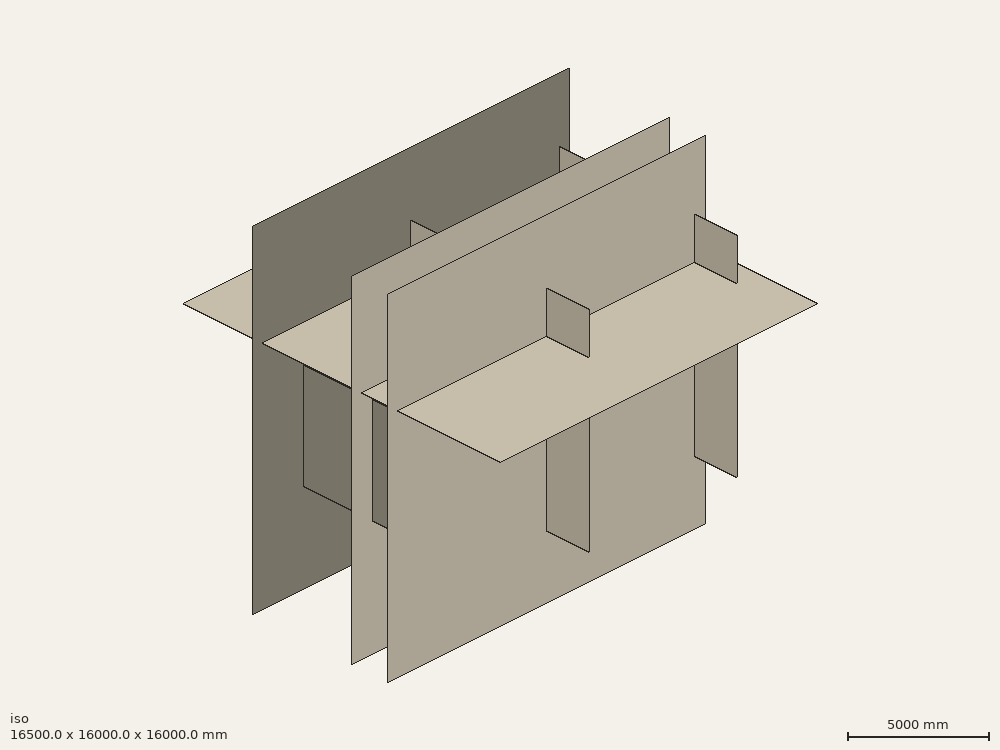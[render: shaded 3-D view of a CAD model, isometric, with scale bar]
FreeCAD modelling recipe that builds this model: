
FCSTD DOCUMENT  (FreeCAD 0.17R13509 (Git))
Label: 1806_fontderibes
License: CreativeCommons Attribution
LicenseURL: http://creativecommons.org/licenses/by/4.0/
objects: App::FeaturePython×61, Part::Part2DObjectPython×29, Part::FeaturePython×25, App::DocumentObjectGroup×16, Sketcher::SketchObject×9, Part::Extrusion×7, App::MaterialObjectPython×6, TechDraw::DrawViewArch×6, App::DocumentObjectGroupPython×4, Spreadsheet::Sheet×1, TechDraw::DrawSVGTemplate×1, Part::Feature×1, TechDraw::DrawViewAnnotation×1, TechDraw::DrawPage×1
note: 79 computed .brp shape members not serialized (recipe doc carries the construction recipe); baked Part::Feature solids carry a one-line shape summary decoded from their .brp

FEATURE [Part::Part2DObjectPython] Rectangle014  label="Area bany"  # Draft 2D object (typed FeaturePython)
  ChamferSize = 0
  Columns = 1
  FilletRadius = 0
  Height = 1500
  Length = 2100
  MakeFace = false
  Placement = pos=(5850,-1750,0) rot=(0,0,1;0rad)
  Rows = 1
FEATURE [Part::Part2DObjectPython] Rectangle017  label="Area magatzem"  # Draft 2D object (typed FeaturePython)
  ChamferSize = 0
  Columns = 1
  FilletRadius = 0
  Height = 1500
  Length = 1800
  MakeFace = false
  Placement = pos=(3950,-1750,0) rot=(0,0,1;0rad)
  Rows = 1
FEATURE [Part::Part2DObjectPython] Rectangle019  label="Area cuina"  # Draft 2D object (typed FeaturePython)
  ChamferSize = 0
  Columns = 1
  FilletRadius = 0
  Height = 1500
  Length = 3600
  MakeFace = false
  Placement = pos=(250,-1750,0) rot=(0,0,1;0rad)
  Rows = 1
FEATURE [Part::Part2DObjectPython] Rectangle064  label="Enva_001"  # Draft 2D object (typed FeaturePython)
  ChamferSize = 0
  Columns = 1
  FilletRadius = 0
  Height = 100
  Length = 7900
  MakeFace = true
  Placement = pos=(150,-5350,0) rot=(0,0,1;0rad)
  Rows = 1
FEATURE [Part::Part2DObjectPython] Rectangle073  label="PC_001"  # Draft 2D object (typed FeaturePython)
  ChamferSize = 0
  Columns = 1
  FilletRadius = 0
  Height = 50
  Length = 900
  MakeFace = true
  Placement = pos=(7150,-1925,0) rot=(0,0,1;0rad)
  Rows = 1
FEATURE [Part::Part2DObjectPython] Rectangle074  label="PC_002"  # Draft 2D object (typed FeaturePython)
  ChamferSize = 0
  Columns = 1
  FilletRadius = 0
  Height = 50
  Length = 900
  MakeFace = true
  Placement = pos=(5150,-1925,0) rot=(0,0,1;0rad)
  Rows = 1
FEATURE [Part::Part2DObjectPython] Rectangle075  label="PC_003"  # Draft 2D object (typed FeaturePython)
  ChamferSize = 0
  Columns = 1
  FilletRadius = 0
  Height = 50
  Length = 1500
  MakeFace = true
  Placement = pos=(2650,-1925,0) rot=(0,0,1;0rad)
  Rows = 1
FEATURE [Part::Part2DObjectPython] Arc  # Draft 2D object (typed FeaturePython)
  FirstAngle = 90
  LastAngle = 180
  MakeFace = false
  Placement = pos=(0,-5350,0) rot=(0,0,1;0rad)
  Radius = 3500
FEATURE [Part::Part2DObjectPython] DWire007  label="Enva_002"  # Draft 2D object (typed FeaturePython)
  ChamferSize = 0
  Closed = true
  End = (1350,-1850,0)
  FilletRadius = 0
  Length = 37800
  MakeFace = true
  Placement = pos=(7448.88,13200.2,0) rot=(0,0,1;0rad)
  Points = (28) [(-6098.88,-14950.2,0),(-7198.88,-14950.2,0),(-7198.88,-13450.2,0),(-3598.88,-13450.2,0),(-3598.88,-14950.2,0),(-4698.88,-14950.2,0),+22 more]
  Start = (1350,-1750,0)
  Subdivisions = 0
FEATURE [Part::Part2DObjectPython] Rectangle  label="Area_sala"  # Draft 2D object (typed FeaturePython)
  ChamferSize = 0
  Columns = 1
  FilletRadius = 0
  Height = 3400
  Length = 7900
  MakeFace = false
  Placement = pos=(150,-5250,0) rot=(0,0,1;0rad)
  Rows = 1
FEATURE [Part::Part2DObjectPython] Rectangle047  label="DV_llit"  # Draft 2D object (typed FeaturePython)
  ChamferSize = 0
  Columns = 1
  FilletRadius = 0
  Height = 1800
  Length = 50
  MakeFace = true
  Placement = pos=(5183.23,-4650,0) rot=(0,0,1;0rad)
  Rows = 1
FEATURE [Part::Extrusion] Extrusion  label="PC03_base"
  Base = -> Rectangle075
  Dir = (0,0,2500)
  DirMode = 0
  FaceMakerClass = Part::FaceMakerBullseye
  LengthFwd = 0
  LengthRev = 0
  Solid = true
  Symmetric = false
FEATURE [Part::Extrusion] Extrusion001  label="PC02_base"
  Base = -> Rectangle074
  Dir = (0,0,2500)
  DirMode = 0
  FaceMakerClass = Part::FaceMakerBullseye
  LengthFwd = 0
  LengthRev = 0
  Solid = true
  Symmetric = false
FEATURE [Part::Extrusion] Extrusion002  label="PC_01_base"
  Base = -> Rectangle073
  Dir = (0,0,2500)
  DirMode = 0
  FaceMakerClass = Part::FaceMakerBullseye
  LengthFwd = 0
  LengthRev = 0
  Solid = true
  Symmetric = false
FEATURE [Part::Part2DObjectPython] DWire  # Draft 2D object (typed FeaturePython)
  ChamferSize = 0
  Closed = true
  End = (250,-1750,0)
  FilletRadius = 0
  Length = 41200
  MakeFace = false
  Placement = pos=(7448.88,13200.2,0) rot=(0,0,1;0rad)
  Points = (28) [(-7198.88,-13450.2,0),(-3598.88,-13450.2,0),(-3598.88,-14950.2,0),(-4698.88,-14950.2,0),(-4698.88,-15050.2,0),(-2998.88,-15050.2,0),+22 more]
  Start = (250,-250,0)
  Subdivisions = 0
FEATURE [Spreadsheet::Sheet] IfcProperties  label="GuBIMClass v.1.2_CA"
  cells = A1=Nivell 1; B1=Nivell 2; C1=Nivell 3; D1=Nivell 4; E1=Codi Complert; F1=Descripció; A2=20; B2=10; C2=10; D2=20; E2=2.10.10.20; F2=Sabates
FEATURE [App::DocumentObjectGroup] IfcPropertiesContainer
  Group = -> [IfcProperties]
FEATURE [Part::Part2DObjectPython] Rectangle061  label="area total_base"  # Draft 2D object (typed FeaturePython)
  ChamferSize = 0
  Columns = 1
  FilletRadius = 0
  Height = 5500
  Length = 8200
  MakeFace = false
  Placement = pos=(4.999e-09,-5500,0) rot=(0,0,1;0rad)
  Rows = 1
FEATURE [Sketcher::SketchObject] Sketch006  label="Area total"
  ExternalGeometry = -> [Rectangle061]
  Placement = pos=(7448.88,13200.2,0) rot=(0,0,1;0rad)
  Support = -> [Rectangle061]
  sketch-geometry (4):
    g0: LineSegment StartX=-7448.88 StartY=-18700.2 StartZ=0 EndX=-7448.88 EndY=-13200.2 EndZ=0
    g1: LineSegment StartX=-7448.88 StartY=-13200.2 StartZ=0 EndX=751.125 EndY=-13200.2 EndZ=0
    g2: LineSegment StartX=751.125 StartY=-13200.2 StartZ=0 EndX=751.125 EndY=-18700.2 EndZ=0
    g3: LineSegment StartX=751.125 StartY=-18700.2 StartZ=0 EndX=-7448.88 EndY=-18700.2 EndZ=0
  constraints (11):
    c: Coincident(g0,g1)
    c: Coincident(g1,g2)
    c: Coincident(g2,g3)
    c: Coincident(g3,g0)
    c: Vertical(g0)
    c: Vertical(g2)
    c: Horizontal(g1)
    c: Horizontal(g3)
    c: DistanceX(g1,g1) = 8200  'A'
    c: DistanceY(g2,g2) = 5500  'B'
    c: Coincident(g-3,g0)
FEATURE [App::DocumentObjectGroup] Group002  label="Àrees"
  Group = -> [Rectangle061,Rectangle019,Rectangle017,Rectangle014,Rectangle,Sketch006]
FEATURE [Sketcher::SketchObject] Sketch007  label="Mur_001_base"
  ExternalGeometry = -> [Sketch006]
  Placement = pos=(7448.88,13200.2,0) rot=(0,0,1;0rad)
  sketch-geometry (2):
    g0: LineSegment StartX=-10948.9 StartY=-18625.2 StartZ=0 EndX=2476.12 EndY=-18625.2 EndZ=0
    g1: LineSegment StartX=2476.12 StartY=-18625.2 StartZ=0 EndX=2476.12 EndY=-15050.2 EndZ=0
  constraints (7):
    c: Coincident(g0,g1)
    c: Horizontal(g0)
    c: Vertical(g1)
    c: DistanceX(g0,g0) = 13425  'A'
    c: DistanceY(g1,g1) = 3575  'B'
    c: DistanceY(g-3,g0) = 75  'C'
    c: DistanceX(g-4,g1) = 1725  'D'
FEATURE [Sketcher::SketchObject] Sketch008  label="Mur_002_base"
  ExternalGeometry = -> [Sketch006]
  Placement = pos=(7448.88,13200.2,0) rot=(0,0,1;0rad)
  sketch-geometry (3):
    g0: LineSegment StartX=-7373.88 StartY=-18550.2 StartZ=0 EndX=-7373.88 EndY=-13275.2 EndZ=0
    g1: LineSegment StartX=-7373.88 StartY=-13275.2 StartZ=0 EndX=676.125 EndY=-13275.2 EndZ=0
    g2: LineSegment StartX=676.125 StartY=-13275.2 StartZ=0 EndX=676.125 EndY=-18550.2 EndZ=0
  constraints (10):
    c: Coincident(g0,g1)
    c: Coincident(g1,g2)
    c: Horizontal(g1)
    c: Vertical(g0)
    c: Vertical(g2)
    c: DistanceY(g0,g-6) = 75
    c: DistanceX(g-6,g0) = 75
    c: Equal(g0,g2)
    c: DistanceX(g1,g-4) = 75
    c: DistanceY(g2,g2) = 5275
FEATURE [Sketcher::SketchObject] Sketch009  label="Solera_base"
  ExternalGeometry = -> [Sketch006]
  MapMode = 2
  Placement = pos=(150,-5350,0) rot=(0,0,1;0rad)
  sketch-geometry (4):
    g0: LineSegment StartX=-5.002e-09 StartY=5200 StartZ=0 EndX=7900 EndY=5200 EndZ=0
    g1: LineSegment StartX=7900 StartY=5200 StartZ=0 EndX=7900 EndY=-5.0004e-08 EndZ=0
    g2: LineSegment StartX=7900 StartY=-5.0004e-08 StartZ=0 EndX=-5.002e-09 EndY=-5.0004e-08 EndZ=0
    g3: LineSegment StartX=-5.002e-09 StartY=-5.0004e-08 StartZ=0 EndX=-5.002e-09 EndY=5200 EndZ=0
  constraints (12):
    c: Coincident(g0,g1)
    c: Coincident(g1,g2)
    c: Coincident(g2,g3)
    c: Coincident(g3,g0)
    c: Horizontal(g0)
    c: Horizontal(g2)
    c: Vertical(g1)
    c: Vertical(g3)
    c: DistanceY(g0,g-6) = 150
    c: DistanceY(g-5,g1) = 150
    c: DistanceX(g0,g-4) = 150
    c: DistanceX(g-6,g2) = 150
FEATURE [Sketcher::SketchObject] Sketch010  label="Sabata_001_base"
  ExternalGeometry = -> [Sketch007]
  MapMode = 2
  Placement = pos=(7448.88,13200.2,0) rot=(0,0,1;0rad)
  sketch-geometry (6):
    g0: LineSegment StartX=-11098.9 StartY=-18225.2 StartZ=0 EndX=2076.12 EndY=-18225.2 EndZ=0
    g1: LineSegment StartX=2076.12 StartY=-18225.2 StartZ=0 EndX=2076.12 EndY=-14900.2 EndZ=0
    g2: LineSegment StartX=2076.12 StartY=-14900.2 StartZ=0 EndX=2876.12 EndY=-14900.2 EndZ=0
    g3: LineSegment StartX=2876.12 StartY=-14900.2 StartZ=0 EndX=2876.12 EndY=-19025.2 EndZ=0
    g4: LineSegment StartX=2876.12 StartY=-19025.2 StartZ=0 EndX=-11098.9 EndY=-19025.2 EndZ=0
    g5: LineSegment StartX=-11098.9 StartY=-19025.2 StartZ=0 EndX=-11098.9 EndY=-18225.2 EndZ=0
  constraints (18):
    c: Coincident(g0,g1)
    c: Coincident(g1,g2)
    c: Coincident(g2,g3)
    c: Coincident(g3,g4)
    c: Horizontal(g4)
    c: Coincident(g4,g5)
    c: Coincident(g5,g0)
    c: Vertical(g5)
    c: Vertical(g3)
    c: Vertical(g1)
    c: Horizontal(g2)
    c: Horizontal(g0)
    c: DistanceX(g1,g-3) = 400
    c: DistanceX(g-3,g2) = 400
    c: DistanceY(g-4,g0) = 400
    c: DistanceY(g4,g-4) = 400
    c: DistanceY(g-3,g1) = 150
    c: DistanceX(g0,g-4) = 150
FEATURE [Sketcher::SketchObject] Sketch011  label="Sabata_002_base"
  ExternalGeometry = -> [Sketch008,Sketch007]
  Placement = pos=(7448.88,13200.2,0) rot=(0,0,1;0rad)
  sketch-geometry (8):
    g0: LineSegment StartX=-7773.88 StartY=-18225.2 StartZ=0 EndX=-7773.88 EndY=-12875.2 EndZ=0
    g1: LineSegment StartX=-7773.88 StartY=-12875.2 StartZ=0 EndX=1076.12 EndY=-12875.2 EndZ=0
    g2: LineSegment StartX=1076.12 StartY=-12875.2 StartZ=0 EndX=1076.12 EndY=-18225.2 EndZ=0
    g3: LineSegment StartX=1076.12 StartY=-18225.2 StartZ=0 EndX=276.125 EndY=-18225.2 EndZ=0
    g4: LineSegment StartX=276.125 StartY=-18225.2 StartZ=0 EndX=276.125 EndY=-13675.2 EndZ=0
    g5: LineSegment StartX=276.125 StartY=-13675.2 StartZ=0 EndX=-6973.88 EndY=-13675.2 EndZ=0
    g6: LineSegment StartX=-6973.88 StartY=-13675.2 StartZ=0 EndX=-6973.88 EndY=-18225.2 EndZ=0
    g7: LineSegment StartX=-6973.88 StartY=-18225.2 StartZ=0 EndX=-7773.88 EndY=-18225.2 EndZ=0
  constraints (25):
    c: Coincident(g0,g1)
    c: Coincident(g1,g2)
    c: Coincident(g2,g3)
    c: Coincident(g3,g4)
    c: Coincident(g4,g5)
    c: Coincident(g5,g6)
    c: Coincident(g6,g7)
    c: Coincident(g7,g0)
    c: Horizontal(g7)
    c: Horizontal(g3)
    c: Horizontal(g5)
    c: Horizontal(g1)
    c: Vertical(g0)
    c: Vertical(g6)
    c: Vertical(g4)
    c: Vertical(g2)
    c: Equal(g6,g4)
    c: Equal(g2,g0)
    c: DistanceY(g-5,g0) = 400
    c: DistanceY(g5,g-5) = 400
    c: DistanceX(g0,g-5) = 400
    c: DistanceX(g-5,g6) = 400
    c: DistanceY(g0,g-6) = -400
    c: Equal(g3,g7)
    c: DistanceX(g3,g-3) = 400
FEATURE [Sketcher::SketchObject] Sketch
  Placement = pos=(8200,-5350,0) rot=(0.57735,0.57735,0.57735;2.0944rad)
  sketch-geometry (24):
    g0: LineSegment StartX=0 StartY=0 StartZ=0 EndX=3400 EndY=0 EndZ=0
    g1: LineSegment StartX=3400 StartY=0 StartZ=0 EndX=3400 EndY=2500 EndZ=0
    g2: LineSegment StartX=3400 StartY=2500 StartZ=0 EndX=0 EndY=2500 EndZ=0
    g3: LineSegment StartX=0 StartY=2500 StartZ=0 EndX=0 EndY=0 EndZ=0
    g4: LineSegment StartX=30 StartY=30 StartZ=0 EndX=3370 EndY=30 EndZ=0
    g5: LineSegment StartX=3370 StartY=30 StartZ=0 EndX=3370 EndY=2470 EndZ=0
    g6: LineSegment StartX=3370 StartY=2470 StartZ=0 EndX=30 EndY=2470 EndZ=0
    g7: LineSegment StartX=30 StartY=2470 StartZ=0 EndX=30 EndY=30 EndZ=0
    g8: LineSegment StartX=33 StartY=33 StartZ=0 EndX=1698.5 EndY=33 EndZ=0
    g9: LineSegment StartX=1698.5 StartY=33 StartZ=0 EndX=1698.5 EndY=2467 EndZ=0
    g10: LineSegment StartX=1698.5 StartY=2467 StartZ=0 EndX=33 EndY=2467 EndZ=0
    g11: LineSegment StartX=33 StartY=2467 StartZ=0 EndX=33 EndY=33 EndZ=0
    g12: LineSegment StartX=103 StartY=103 StartZ=0 EndX=1628.5 EndY=103 EndZ=0
    g13: LineSegment StartX=1628.5 StartY=103 StartZ=0 EndX=1628.5 EndY=2397 EndZ=0
    g14: LineSegment StartX=1628.5 StartY=2397 StartZ=0 EndX=103 EndY=2397 EndZ=0
    g15: LineSegment StartX=103 StartY=2397 StartZ=0 EndX=103 EndY=103 EndZ=0
    g16: LineSegment StartX=1701.5 StartY=33 StartZ=0 EndX=3367 EndY=33 EndZ=0
    g17: LineSegment StartX=3367 StartY=33 StartZ=0 EndX=3367 EndY=2467 EndZ=0
    g18: LineSegment StartX=3367 StartY=2467 StartZ=0 EndX=1701.5 EndY=2467 EndZ=0
    g19: LineSegment StartX=1701.5 StartY=2467 StartZ=0 EndX=1701.5 EndY=33 EndZ=0
    g20: LineSegment StartX=1771.5 StartY=103 StartZ=0 EndX=3297 EndY=103 EndZ=0
    g21: LineSegment StartX=3297 StartY=103 StartZ=0 EndX=3297 EndY=2397 EndZ=0
    g22: LineSegment StartX=3297 StartY=2397 StartZ=0 EndX=1771.5 EndY=2397 EndZ=0
    g23: LineSegment StartX=1771.5 StartY=2397 StartZ=0 EndX=1771.5 EndY=103 EndZ=0
  constraints (71):
    c: Coincident(g0,g1)
    c: Coincident(g1,g2)
    c: Coincident(g2,g3)
    c: Coincident(g3,g0)
    c: Horizontal(g0)
    c: Horizontal(g2)
    c: Vertical(g1)
    c: Vertical(g3)
    c: Coincident(g4,g5)
    c: Coincident(g5,g6)
    c: Coincident(g6,g7)
    c: Coincident(g7,g4)
    c: Horizontal(g4)
    c: Horizontal(g6)
    c: Vertical(g5)
    c: Vertical(g7)
    c: DistanceY(g1) = 2500  'Height'
    c: DistanceX(g0) = 3400  'Width'
    c: DistanceY(g6,g2) = 30
    c: DistanceX(g2,g6) = 30
    c: DistanceX(g4,g0) = 30
    c: DistanceY(g0,g4) = 30
    c: Coincident(g0,g-1)
    c: Coincident(g8,g9)
    c: Coincident(g9,g10)
    c: Coincident(g10,g11)
    c: Coincident(g11,g8)
    c: Horizontal(g8)
    c: Horizontal(g10)
    c: Vertical(g9)
    c: Vertical(g11)
    c: Coincident(g12,g13)
    c: Coincident(g13,g14)
    c: Coincident(g14,g15)
    c: Coincident(g15,g12)
    c: Horizontal(g12)
    c: Horizontal(g14)
    c: Vertical(g13)
    c: Vertical(g15)
    c: Coincident(g16,g17)
    c: Coincident(g17,g18)
    c: Coincident(g18,g19)
    c: Coincident(g19,g16)
    c: Horizontal(g16)
    c: Horizontal(g18)
    c: Vertical(g17)
    c: Vertical(g19)
    c: Coincident(g20,g21)
    c: Coincident(g21,g22)
    c: Coincident(g22,g23)
    c: Coincident(g23,g20)
    c: Horizontal(g20)
    c: Horizontal(g22)
    c: Vertical(g21)
    c: Vertical(g23)
    c: DistanceY(g8,g12) = 70
    c: DistanceX(g8,g12) = 70
    c: DistanceX(g21,g17) = 70
    c: DistanceY(g21,g17) = 70
    c: DistanceX(g16,g20) = 70
    c: DistanceX(g14,g10) = 70
    c: Equal(g22,g14)
    c: DistanceY(g8,g16) = 0
    c: DistanceY(g10,g18) = 0
    c: DistanceX(g4,g8) = 3
    c: DistanceY(g4,g8) = 3
    c: DistanceX(g6,g18) = -3
    c: DistanceY(g6,g18) = -3
    c: DistanceX(g9,g19) = 3
    c: PointOnObject(g13,g22)
    c: PointOnObject(g12,g20)
FEATURE [Sketcher::SketchObject] Sketch012
  Placement = pos=(1e-12,-1850,0) rot=(0.57735,-0.57735,-0.57735;2.0944rad)
  sketch-geometry (24):
    g0: LineSegment StartX=0 StartY=0 StartZ=0 EndX=3500 EndY=0 EndZ=0
    g1: LineSegment StartX=3500 StartY=0 StartZ=0 EndX=3500 EndY=2500 EndZ=0
    g2: LineSegment StartX=3500 StartY=2500 StartZ=0 EndX=0 EndY=2500 EndZ=0
    g3: LineSegment StartX=0 StartY=2500 StartZ=0 EndX=0 EndY=0 EndZ=0
    g4: LineSegment StartX=30 StartY=30 StartZ=0 EndX=3470 EndY=30 EndZ=0
    g5: LineSegment StartX=3470 StartY=30 StartZ=0 EndX=3470 EndY=2470 EndZ=0
    g6: LineSegment StartX=3470 StartY=2470 StartZ=0 EndX=30 EndY=2470 EndZ=0
    g7: LineSegment StartX=30 StartY=2470 StartZ=0 EndX=30 EndY=30 EndZ=0
    g8: LineSegment StartX=33 StartY=33 StartZ=0 EndX=1748.5 EndY=33 EndZ=0
    g9: LineSegment StartX=1748.5 StartY=33 StartZ=0 EndX=1748.5 EndY=2467 EndZ=0
    g10: LineSegment StartX=1748.5 StartY=2467 StartZ=0 EndX=33 EndY=2467 EndZ=0
    g11: LineSegment StartX=33 StartY=2467 StartZ=0 EndX=33 EndY=33 EndZ=0
    g12: LineSegment StartX=103 StartY=103 StartZ=0 EndX=1678.5 EndY=103 EndZ=0
    g13: LineSegment StartX=1678.5 StartY=103 StartZ=0 EndX=1678.5 EndY=2397 EndZ=0
    g14: LineSegment StartX=1678.5 StartY=2397 StartZ=0 EndX=103 EndY=2397 EndZ=0
    g15: LineSegment StartX=103 StartY=2397 StartZ=0 EndX=103 EndY=103 EndZ=0
    g16: LineSegment StartX=1751.5 StartY=33 StartZ=0 EndX=3467 EndY=33 EndZ=0
    g17: LineSegment StartX=3467 StartY=33 StartZ=0 EndX=3467 EndY=2467 EndZ=0
    g18: LineSegment StartX=3467 StartY=2467 StartZ=0 EndX=1751.5 EndY=2467 EndZ=0
    g19: LineSegment StartX=1751.5 StartY=2467 StartZ=0 EndX=1751.5 EndY=33 EndZ=0
    g20: LineSegment StartX=1821.5 StartY=103 StartZ=0 EndX=3397 EndY=103 EndZ=0
    g21: LineSegment StartX=3397 StartY=103 StartZ=0 EndX=3397 EndY=2397 EndZ=0
    g22: LineSegment StartX=3397 StartY=2397 StartZ=0 EndX=1821.5 EndY=2397 EndZ=0
    g23: LineSegment StartX=1821.5 StartY=2397 StartZ=0 EndX=1821.5 EndY=103 EndZ=0
  constraints (71):
    c: Coincident(g0,g1)
    c: Coincident(g1,g2)
    c: Coincident(g2,g3)
    c: Coincident(g3,g0)
    c: Horizontal(g0)
    c: Horizontal(g2)
    c: Vertical(g1)
    c: Vertical(g3)
    c: Coincident(g4,g5)
    c: Coincident(g5,g6)
    c: Coincident(g6,g7)
    c: Coincident(g7,g4)
    c: Horizontal(g4)
    c: Horizontal(g6)
    c: Vertical(g5)
    c: Vertical(g7)
    c: DistanceY(g1) = 2500  'Height'
    c: DistanceX(g0) = 3500  'Width'
    c: DistanceY(g6,g2) = 30
    c: DistanceX(g2,g6) = 30
    c: DistanceX(g4,g0) = 30
    c: DistanceY(g0,g4) = 30
    c: Coincident(g0,g-1)
    c: Coincident(g8,g9)
    c: Coincident(g9,g10)
    c: Coincident(g10,g11)
    c: Coincident(g11,g8)
    c: Horizontal(g8)
    c: Horizontal(g10)
    c: Vertical(g9)
    c: Vertical(g11)
    c: Coincident(g12,g13)
    c: Coincident(g13,g14)
    c: Coincident(g14,g15)
    c: Coincident(g15,g12)
    c: Horizontal(g12)
    c: Horizontal(g14)
    c: Vertical(g13)
    c: Vertical(g15)
    c: Coincident(g16,g17)
    c: Coincident(g17,g18)
    c: Coincident(g18,g19)
    c: Coincident(g19,g16)
    c: Horizontal(g16)
    c: Horizontal(g18)
    c: Vertical(g17)
    c: Vertical(g19)
    c: Coincident(g20,g21)
    c: Coincident(g21,g22)
    c: Coincident(g22,g23)
    c: Coincident(g23,g20)
    c: Horizontal(g20)
    c: Horizontal(g22)
    c: Vertical(g21)
    c: Vertical(g23)
    c: DistanceY(g8,g12) = 70
    c: DistanceX(g8,g12) = 70
    c: DistanceX(g21,g17) = 70
    c: DistanceY(g21,g17) = 70
    c: DistanceX(g16,g20) = 70
    c: DistanceX(g14,g10) = 70
    c: Equal(g22,g14)
    c: DistanceY(g8,g16) = 0
    c: DistanceY(g10,g18) = 0
    c: DistanceX(g4,g8) = 3
    c: DistanceY(g4,g8) = 3
    c: DistanceX(g6,g18) = -3
    c: DistanceY(g6,g18) = -3
    c: DistanceX(g9,g19) = 3
    c: PointOnObject(g13,g22)
    c: PointOnObject(g12,g20)
FEATURE [App::MaterialObjectPython] Material  label="Formigó H-25"  # material (typed FeaturePython)
  Material = Color=(0.9411764705882353, 0.9411764705882353, 0.9411764705882353),DiffuseColor=(0.9411764740943909, 0.9411764740943909, 0.9411764740943909),+3 more (map truncated)
  Transparency = 0
FEATURE [Part::FeaturePython] Structure  label="Solera"  # WARN: FeaturePython — macro-defined, semantics opaque (R4)
  Base = -> Sketch009
  FaceMaker = 0
  Height = 200
  HorizontalArea = 41080000
  Length = 0
  Material = -> Material
  MoveWithHost = false
  Nodes = (4) [(-7298.88,-13350.2,0),(601.125,-13350.2,0),(601.125,-18550.2,0),(-7298.88,-18550.2,0)]
  NodesOffset = 0
  Normal = (0,0,0)
  PerimeterLength = 26200
  Placement = pos=(0,0,-300) rot=(0,0,1;0rad)
  Role = 3
  VerticalArea = 5240000
  Width = 100
FEATURE [Part::FeaturePython] Structure001  label="Sabata_001"  # Arch/BIM object (typed FeaturePython)
  Base = -> Sketch010
  FaceMaker = 0
  Height = 400
  HorizontalArea = 13840000
  IfcProperties = -> IfcProperties
  Length = 0
  Material = -> Material
  MoveWithHost = false
  Nodes = (2) [(-2863.62,-18210.5,-313.595),(-2863.62,-18210.5,86.4045)]
  NodesOffset = 0
  Normal = (0,0,0)
  PerimeterLength = 36200
  Placement = pos=(0,0,-500) rot=(0,0,1;0rad)
  Role = 7
  VerticalArea = 14480000
  Width = 100
FEATURE [Part::FeaturePython] Structure002  label="Sabata_002"  # Arch/BIM object (typed FeaturePython)
  Base = -> Sketch011
  FaceMaker = 0
  Height = 400
  HorizontalArea = 14360000
  IfcAttributes = IfcUID=3Gc_ZFGLuHwBQVF1N2v1hf
  IfcProperties = -> IfcProperties
  Length = 0
  Material = -> Material
  MoveWithHost = false
  Nodes = (2) [(-3348.88,-14662.1,-232.343),(-3348.88,-14662.1,-632.343)]
  NodesOffset = 0
  Normal = (0,0,0)
  PerimeterLength = 37500
  Placement = pos=(1e-12,0,-500) rot=(0,0,1;0rad)
  Role = 7
  VerticalArea = 1.5e+07
  Width = 100
FEATURE [App::DocumentObjectGroup] Group008  label="Estructura"
  Group = -> [Structure,Structure001,Structure002]
FEATURE [Part::FeaturePython] Structure003  label="Forjat coberta"  # WARN: FeaturePython — macro-defined, semantics opaque (R4)
  Base = -> Sketch006
  FaceMaker = 0
  Height = 200
  HorizontalArea = 45100000
  Length = 0
  Material = -> Material
  MoveWithHost = false
  Nodes = (4) [(-7448.88,-18700.2,0),(-7448.88,-13200.2,0),(751.125,-13200.2,0),(751.125,-18700.2,0)]
  NodesOffset = 0
  Normal = (0,0,1)
  PerimeterLength = 27400
  Placement = pos=(0,0,2500) rot=(0,0,1;0rad)
  Role = 3
  VerticalArea = 5480000
  Width = 100
FEATURE [Part::FeaturePython] Wall007  label="Muret coberta"  # WARN: FeaturePython — macro-defined, semantics opaque (R4)
  Align = 0
  Base = -> Sketch006
  Face = 0
  Height = 400
  HorizontalArea = 5.32e+06
  Length = 27400
  Material = -> Material
  MoveWithHost = false
  Normal = (0,0,1)
  PerimeterLength = 27400
  Placement = pos=(0,0,2700) rot=(0,0,1;0rad)
  Role = 1
  VerticalArea = 21280000
  Width = 200
FEATURE [App::DocumentObjectGroup] Group009  label="PC_EST"
  Group = -> [Structure003,Wall007]
FEATURE [App::DocumentObjectGroupPython] Floor001  label="Coberta"  # scripted group (container) (typed FeaturePython)
  Area = 0
  Group = -> [Group009]
  Height = 0
FEATURE [App::MaterialObjectPython] Material001  label="Gero"  # material (typed FeaturePython)
  Description = Maó calat de forats perpendiculars al pla (V>10%)
  Material = Color=(1.0, 0.5647058823529412, 0.1843137254901961),Description=Maó calat de forats perpendiculars al pla (V>10%),+4 more (map truncated)
  Transparency = 0
FEATURE [Part::FeaturePython] Wall001  label="Mur_002"  # Arch/BIM object (typed FeaturePython)
  Align = 2
  Base = -> Sketch008
  Description = Mur de gero
  Face = 0
  Height = 3000
  HorizontalArea = 2.79e+06
  IfcAttributes = IfcUID=0CiF5mFoOHwBg6F1N2v1hf
  Length = 18600
  Material = -> Material001
  MoveWithHost = false
  Normal = (0,0,0)
  PerimeterLength = 37500
  Placement = pos=(0,0,-500) rot=(0,0,1;0rad)
  Role = 1
  VerticalArea = 7.8e+07
  Width = 150
FEATURE [Part::FeaturePython] Wall002  label="Mur_001"  # Arch/BIM object (typed FeaturePython)
  Align = 2
  Base = -> Sketch007
  Description = Mur de gero
  Face = 0
  Height = 3000
  HorizontalArea = 2977500
  IfcAttributes = IfcUID=0ChshFFoOHwBdvF1N2v1hf
  Length = 17000
  Material = -> Material001
  MoveWithHost = false
  Normal = (0,0,0)
  PerimeterLength = 34300
  Placement = pos=(0,0,-500) rot=(0,0,1;0rad)
  Role = 1
  VerticalArea = 99120000
  Width = 150
FEATURE [App::DocumentObjectGroup] Group003  label="Murs Ext"
  Group = -> [Wall002,Wall001]
FEATURE [Part::FeaturePython] Window  label="F01_002"  # WARN: FeaturePython — macro-defined, semantics opaque (R4)
  Area = 8500000
  Base = -> Sketch
  Height = 2500
  HoleDepth = 0
  HoleWire = 0
  HorizontalArea = 0
  Hosts = -> [Wall001]
  LouvreSpacing = 0
  LouvreWidth = 0
  MoveWithHost = true
  Normal = (-1,0,0)
  Opening = 0
  PerimeterLength = 0
  Preset = 5
  Role = 1
  SymbolElevation = false
  SymbolPlan = false
  VerticalArea = 0
  Width = 3400
  WindowParts = OuterFrame | Frame | Wire0,Wire1 | 150.0 | 0.0 | LeftFrame | Frame | Wire2,Wire3 | 30.0 | 75.0 | LeftGlass | Glass panel | Wire3 | 3.0 | 90.0 | RightFrame | Frame | Wire4,Wire5 | 30.0 | 105.0 | RightGlass | Glass panel | Wire5 | 3.0 | 120.0
  WindowParts1 = 0
FEATURE [Part::FeaturePython] Window001  label="F01_001"  # WARN: FeaturePython — macro-defined, semantics opaque (R4)
  Area = 8750000
  Base = -> Sketch012
  Height = 2500
  HoleDepth = 0
  HoleWire = 0
  HorizontalArea = 0
  Hosts = -> [Wall001]
  LouvreSpacing = 0
  LouvreWidth = 0
  MoveWithHost = true
  Normal = (1,0,0)
  Opening = 0
  PerimeterLength = 0
  Preset = 5
  Role = 1
  SymbolElevation = false
  SymbolPlan = false
  VerticalArea = 0
  Width = 3500
  WindowParts = OuterFrame | Frame | Wire0,Wire1 | 150.0 | 0.0 | LeftFrame | Frame | Wire2,Wire3 | 30.0 | 75.0 | LeftGlass | Glass panel | Wire3 | 3.0 | 90.0 | RightFrame | Frame | Wire4,Wire5 | 30.0 | 105.0 | RightGlass | Glass panel | Wire5 | 3.0 | 120.0
  WindowParts1 = 0
FEATURE [Sketcher::SketchObject] Sketch013
  ExternalGeometry = -> [Wall002]
  MapMode = 5
  Placement = pos=(7448.88,-5500,-500) rot=(1,0,0;1.5708rad)
  sketch-geometry (8):
    g0: LineSegment StartX=-5073.88 StartY=2100 StartZ=0 EndX=-2223.88 EndY=2100 EndZ=0
    g1: LineSegment StartX=-2223.88 StartY=2100 StartZ=0 EndX=-2223.88 EndY=1400 EndZ=0
    g2: LineSegment StartX=-2223.88 StartY=1400 StartZ=0 EndX=-5073.88 EndY=1400 EndZ=0
    g3: LineSegment StartX=-5073.88 StartY=1400 StartZ=0 EndX=-5073.88 EndY=2100 EndZ=0
    g4: LineSegment StartX=-5043.88 StartY=2070 StartZ=0 EndX=-2253.88 EndY=2070 EndZ=0
    g5: LineSegment StartX=-2253.88 StartY=2070 StartZ=0 EndX=-2253.88 EndY=1430 EndZ=0
    g6: LineSegment StartX=-2253.88 StartY=1430 StartZ=0 EndX=-5043.88 EndY=1430 EndZ=0
    g7: LineSegment StartX=-5043.88 StartY=1430 StartZ=0 EndX=-5043.88 EndY=2070 EndZ=0
  constraints (24):
    c: Coincident(g0,g1)
    c: Coincident(g1,g2)
    c: Coincident(g2,g3)
    c: Coincident(g3,g0)
    c: Horizontal(g0)
    c: Horizontal(g2)
    c: Vertical(g1)
    c: Vertical(g3)
    c: Coincident(g4,g5)
    c: Coincident(g5,g6)
    c: Coincident(g6,g7)
    c: Coincident(g7,g4)
    c: Horizontal(g4)
    c: Horizontal(g6)
    c: Vertical(g5)
    c: Vertical(g7)
    c: DistanceX(g0,g4) = 30
    c: DistanceX(g5,g1) = 30
    c: DistanceY(g4,g0) = 30
    c: DistanceY(g2,g6) = 30
    c: DistanceX(g2,g2) = 2850
    c: DistanceY(g1,g1) = 700
    c: DistanceX(g-4,g0) = 5875
    c: DistanceY(g0,g-4) = 900
FEATURE [App::MaterialObjectPython] Material002  label="Fusta vernissada"  # material (typed FeaturePython)
  Material = Color=(0.8117647058823529, 0.403921568627451, 0.0),DiffuseColor=(0.8117647171020508, 0.40392157435417175, 0.0),Name=Fusta vernissada,Transparency=0,+1 more (map truncated)
  Transparency = 0
FEATURE [Part::FeaturePython] Wall004  label="DIV_03"  # WARN: FeaturePython — macro-defined, semantics opaque (R4)
  Align = 2
  Base = -> Rectangle047
  Description = Divisió Vertical de fusta
  Face = 0
  Height = 1800
  HorizontalArea = 90000
  Length = 0
  Material = -> Material002
  MoveWithHost = false
  Normal = (0,0,0)
  PerimeterLength = 3700
  Role = 1
  VerticalArea = 6.66e+06
  Width = 100
FEATURE [Part::FeaturePython] Component  label="PC03"  # Arch/BIM object (typed FeaturePython)
  Base = -> Extrusion
  Description = Porta corredissa
  HorizontalArea = 0
  IfcAttributes = IfcUID=0CidWIFoOHwBntF1N2v1hf
  Material = -> Material002
  MoveWithHost = false
  PerimeterLength = 0
  Role = 6
  VerticalArea = 0
FEATURE [Part::FeaturePython] Component003  label="PC02"  # Arch/BIM object (typed FeaturePython)
  Base = -> Extrusion001
  Description = Porta corredissa
  HorizontalArea = 0
  IfcAttributes = IfcUID=0CizUUFoOHw8DBF1N2v1hf
  Material = -> Material002
  MoveWithHost = false
  PerimeterLength = 0
  Role = 6
  VerticalArea = 0
FEATURE [Part::FeaturePython] Component004  label="PC01"  # Arch/BIM object (typed FeaturePython)
  Base = -> Extrusion002
  Description = Porta corredissa
  HorizontalArea = 0
  IfcAttributes = IfcUID=0CjH0XFoOHwA19F1N2v1hf
  Material = -> Material002
  MoveWithHost = false
  PerimeterLength = 0
  Role = 6
  VerticalArea = 0
FEATURE [App::DocumentObjectGroup] Group004  label="Fusteries Int"
  Group = -> [Rectangle073,Rectangle074,Rectangle075,Component,Component003,Component004]
FEATURE [App::MaterialObjectPython] Material003  label="Acer Corten"  # material (typed FeaturePython)
  Material = Color=(0.6666666666666666, 0.0, 0.0); DiffuseColor=(0.6666666865348816, 0.0, 0.0); Name=Acer Corten; Transparency=0; ViewColor=(0.6666666666666666, 0.0, 0.0)
  Transparency = 0
FEATURE [Part::FeaturePython] Component006  label="S01_001"  # Arch/BIM object (typed FeaturePython)
  HorizontalArea = 0
  IfcAttributes = IfcUID=1ywVmYGP8Hw8cSF1N2v1hf
  Material = -> Material003
  MoveWithHost = false
  PerimeterLength = 0
  Placement = pos=(8200,-1850,0) rot=(0,0,-1;1.5708rad)
  Role = 13
  VerticalArea = 0
FEATURE [Part::FeaturePython] Component007  label="S01_002"  # Arch/BIM object (typed FeaturePython)
  CloneOf = -> Component006
  Description = Fusteria d'alumini corredissa
  HorizontalArea = 0
  IfcAttributes = IfcUID=1z4270GP8Hw9ipF1N2v1hf
  Material = -> Material003
  MoveWithHost = false
  PerimeterLength = 0
  Placement = pos=(8200,-5250,0) rot=(0,0,-1;1.5708rad)
  Role = 13
  VerticalArea = 0
FEATURE [Part::FeaturePython] Component008  label="S02"  # Arch/BIM object (typed FeaturePython)
  Description = Fusteria d'alumini corredissa
  HorizontalArea = 0
  IfcAttributes = IfcUID=1z4271GP8HwBOmF1N2v1hf
  Material = -> Material003
  MoveWithHost = false
  PerimeterLength = 0
  Placement = pos=(-3350,-5350,0) rot=(0,0,1;0rad)
  Role = 13
  VerticalArea = 0
FEATURE [App::DocumentObjectGroup] Group006  label="Serralleria"
  Group = -> [Component006,Component007,Component008]
FEATURE [App::MaterialObjectPython] Material004  label="Formigó lliscat"  # material (typed FeaturePython)
  Material = Color=(0.9411764705882353, 0.9411764705882353, 0.9411764705882353),DiffuseColor=(0.9411764740943909, 0.9411764740943909, 0.9411764740943909),+3 more (map truncated)
  Transparency = 0
FEATURE [App::MaterialObjectPython] Material005  label="Enguixat"  # material (typed FeaturePython)
  Material = Color=(1.0, 1.0, 1.0); DiffuseColor=(1.0, 1.0, 1.0); Name=Enguixat; Transparency=0; ViewColor=(1.0, 1.0, 1.0)
  Transparency = 0
FEATURE [Part::FeaturePython] Wall  label="DIV_02"  # WARN: FeaturePython — macro-defined, semantics opaque (R4)
  Align = 2
  Base = -> DWire007
  Description = Envà de 10
  Face = 0
  Height = 2600
  HorizontalArea = 1880000
  Length = 0
  Material = -> Material005
  MoveWithHost = false
  Normal = (0,0,0)
  PerimeterLength = 37800
  Placement = pos=(0,0,-100) rot=(0,0,1;0rad)
  Role = 1
  VerticalArea = 98280000
  Width = 100
FEATURE [Part::FeaturePython] Wall003  label="DIV_01"  # WARN: FeaturePython — macro-defined, semantics opaque (R4)
  Align = 2
  Base = -> Rectangle064
  Description = Envà de 10
  Face = 0
  Height = 2600
  HorizontalArea = 1075000
  Length = 0
  Material = -> Material005
  MoveWithHost = false
  Normal = (0,0,0)
  PerimeterLength = 16000
  Placement = pos=(0,0,-100) rot=(0,0,1;0rad)
  Role = 1
  VerticalArea = 37750000
  Width = 100
FEATURE [App::DocumentObjectGroup] Group005  label="Murs Int"
  Group = -> [Wall,Wall003,Wall004]
FEATURE [Part::FeaturePython] Window002  label="F02"  # WARN: FeaturePython — macro-defined, semantics opaque (R4)
  Area = 0
  Base = -> Sketch013
  Height = 0
  HoleDepth = 0
  HoleWire = 0
  HorizontalArea = 0
  Hosts = -> [Wall002,Wall003]
  LouvreSpacing = 0
  LouvreWidth = 0
  MoveWithHost = true
  Normal = (0,1,0)
  Opening = 0
  PerimeterLength = 0
  Placement = pos=(2e-12,-250,0) rot=(0,0,1;0rad)
  Preset = 0
  Role = 1
  SymbolElevation = false
  SymbolPlan = false
  VerticalArea = 0
  Width = 0
  WindowParts = Marc | Frame | Wire0,Wire1 | 500.0 | 0.0 | Vidre | Glass panel | Wire1 | 20.0 | 0.0
  WindowParts1 = 0
FEATURE [App::DocumentObjectGroupPython] MaterialContainer  label="Materials"  # scripted group (container) (typed FeaturePython)
  Group = -> [Material,Material001,Material002,Material003,Material004,Material005]
FEATURE [Part::Part2DObjectPython] Rectangle077  # Draft 2D object (typed FeaturePython)
  ChamferSize = 0
  Columns = 1
  FilletRadius = 0
  Height = 500
  Length = 500
  MakeFace = true
  Placement = pos=(-4000,-6000,0) rot=(0,0,1;0rad)
  Rows = 1
FEATURE [Part::Part2DObjectPython] Rectangle078  # Draft 2D object (typed FeaturePython)
  ChamferSize = 0
  Columns = 1
  FilletRadius = 0
  Height = 500
  Length = 500
  MakeFace = true
  Placement = pos=(-4500,-6500,0) rot=(0,0,1;0rad)
  Rows = 1
FEATURE [Part::Part2DObjectPython] Rectangle079  # Draft 2D object (typed FeaturePython)
  ChamferSize = 0
  Columns = 1
  FilletRadius = 0
  Height = 500
  Length = 500
  MakeFace = true
  Placement = pos=(10000,-6000,0) rot=(0,0,1;0rad)
  Rows = 1
FEATURE [Part::Part2DObjectPython] Rectangle080  # Draft 2D object (typed FeaturePython)
  ChamferSize = 0
  Columns = 1
  FilletRadius = 0
  Height = 500
  Length = 500
  MakeFace = true
  Placement = pos=(10500,-6500,0) rot=(0,0,1;0rad)
  Rows = 1
FEATURE [Part::Part2DObjectPython] Rectangle081  # Draft 2D object (typed FeaturePython)
  ChamferSize = 0
  Columns = 1
  FilletRadius = 0
  Height = 500
  Length = 500
  MakeFace = true
  Placement = pos=(10000,-1850,0) rot=(0,0,1;0rad)
  Rows = 1
FEATURE [Part::Part2DObjectPython] Rectangle082  # Draft 2D object (typed FeaturePython)
  ChamferSize = 0
  Columns = 1
  FilletRadius = 0
  Height = 500
  Length = 500
  MakeFace = true
  Placement = pos=(10500,-1350,0) rot=(0,0,1;0rad)
  Rows = 1
FEATURE [Part::Part2DObjectPython] Rectangle083  # Draft 2D object (typed FeaturePython)
  ChamferSize = 0
  Columns = 1
  FilletRadius = 0
  Height = 500
  Length = 500
  MakeFace = true
  Placement = pos=(8200,5e-08,0) rot=(0,0,1;0rad)
  Rows = 1
FEATURE [Part::Part2DObjectPython] Rectangle084  # Draft 2D object (typed FeaturePython)
  ChamferSize = 0
  Columns = 1
  FilletRadius = 0
  Height = 500
  Length = 500
  MakeFace = true
  Placement = pos=(8700,500,0) rot=(0,0,1;0rad)
  Rows = 1
FEATURE [Part::Part2DObjectPython] Rectangle085  # Draft 2D object (typed FeaturePython)
  ChamferSize = 0
  Columns = 1
  FilletRadius = 0
  Height = 500
  Length = 500
  MakeFace = true
  Placement = pos=(-1000,500,0) rot=(0,0,1;0rad)
  Rows = 1
FEATURE [Part::Part2DObjectPython] Rectangle086  # Draft 2D object (typed FeaturePython)
  ChamferSize = 0
  Columns = 1
  FilletRadius = 0
  Height = 500
  Length = 500
  MakeFace = true
  Placement = pos=(-500,5e-08,0) rot=(0,0,1;0rad)
  Rows = 1
FEATURE [App::DocumentObjectGroup] Construction
  Group = -> [Rectangle077,Rectangle078,Rectangle079,Rectangle080,Rectangle081,Rectangle082,Rectangle083,Rectangle084,Rectangle085,Rectangle086]
FEATURE [App::FeaturePython] Dimension004  # Draft dimension (typed FeaturePython)
  Diameter = false
  Dimline = (8699,-1950,0)
  Direction = (0,0,0)
  Distance = 3400
  End = (8200,-5350,0)
  Normal = (0,0,1)
  Start = (8200,-1950,0)
FEATURE [App::FeaturePython] Dimension005  # Draft dimension (typed FeaturePython)
  Diameter = false
  Dimline = (250,-1094.6,0)
  Direction = (0,0,0)
  Distance = 250
  End = (250,-1094.6,0)
  Normal = (0,0,1)
  Start = (9.999e-09,-1094.6,0)
FEATURE [App::FeaturePython] Dimension006  # Draft dimension (typed FeaturePython)
  Diameter = false
  Dimline = (250,-1094.6,0)
  Direction = (0,0,0)
  Distance = 3600
  End = (3850,-1094.6,0)
  Normal = (0,0,1)
  Start = (250,-1094.6,0)
FEATURE [App::FeaturePython] Dimension007  # Draft dimension (typed FeaturePython)
  Diameter = false
  Dimline = (250,-1094.6,0)
  Direction = (0,0,0)
  Distance = 100
  End = (3950,-1094.6,0)
  Normal = (0,0,1)
  Start = (3850,-1094.6,0)
FEATURE [App::FeaturePython] Dimension008  # Draft dimension (typed FeaturePython)
  Diameter = false
  Dimline = (250,-1094.6,0)
  Direction = (0,0,0)
  Distance = 1800
  End = (5750,-1094.6,0)
  Normal = (0,0,1)
  Start = (3950,-1094.6,0)
FEATURE [App::FeaturePython] Dimension009  # Draft dimension (typed FeaturePython)
  Diameter = false
  Dimline = (250,-1094.6,0)
  Direction = (0,0,0)
  Distance = 100
  End = (5850,-1094.6,0)
  Normal = (0,0,1)
  Start = (5750,-1094.6,0)
FEATURE [App::FeaturePython] Dimension010  # Draft dimension (typed FeaturePython)
  Diameter = false
  Dimline = (250,-1094.6,0)
  Direction = (0,0,0)
  Distance = 2100
  End = (7950,-1094.6,0)
  Normal = (0,0,1)
  Start = (5850,-1094.6,0)
FEATURE [App::FeaturePython] Dimension011  # Draft dimension (typed FeaturePython)
  Diameter = false
  Dimline = (250,-1094.6,0)
  Direction = (0,0,0)
  Distance = 250
  End = (8200,-1094.6,0)
  Normal = (0,0,1)
  Start = (7950,-1094.6,0)
FEATURE [App::FeaturePython] Dimension012  # Draft dimension (typed FeaturePython)
  Diameter = false
  Dimline = (10500,-6500,0)
  Direction = (0,0,0)
  Distance = 13500
  End = (10000,-5500,0)
  Normal = (0,0,1)
  Start = (-3500,-5500,0)
FEATURE [App::FeaturePython] Dimension014  # Draft dimension (typed FeaturePython)
  Diameter = false
  Dimline = (2375,-6000,0)
  Direction = (0,0,0)
  Distance = 2850
  End = (5225,-5750,0)
  Normal = (0,0,1)
  Start = (2375,-5750,0)
FEATURE [App::FeaturePython] Dimension017  # Draft dimension (typed FeaturePython)
  Diameter = false
  Dimline = (-500,-1850,0)
  Direction = (0,0,0)
  Distance = 3400
  End = (9.999e-09,-5250,0)
  Normal = (0,0,1)
  Start = (9.999e-09,-1850,0)
FEATURE [App::FeaturePython] Dimension018  # Draft dimension (typed FeaturePython)
  Diameter = false
  Dimline = (-500,-5250,0)
  Direction = (0,0,0)
  Distance = 250
  End = (9.998e-09,-5500,0)
  Normal = (0,0,1)
  Start = (9.999e-09,-5250,0)
FEATURE [App::FeaturePython] Dimension019  # Draft dimension (typed FeaturePython)
  Diameter = false
  Dimline = (800,-0.00016282,0)
  Direction = (0,0,0)
  Distance = 1500
  End = (800,-250,0)
  Normal = (0,0,1)
  Start = (800,-1750,0)
FEATURE [App::FeaturePython] Dimension020  # Draft dimension (typed FeaturePython)
  Diameter = false
  Dimline = (800,-0.00016282,0)
  Direction = (0,0,0)
  Distance = 250
  End = (800,-0.00016282,0)
  Normal = (0,0,1)
  Start = (800,-250,0)
FEATURE [App::FeaturePython] Dimension021  # Draft dimension (typed FeaturePython)
  Diameter = false
  Dimline = (800,-5250,0)
  Direction = (0,0,0)
  Distance = 100
  End = (800,-1850,0)
  Normal = (0,0,1)
  Start = (800,-1750,0)
FEATURE [App::FeaturePython] Dimension022  # Draft dimension (typed FeaturePython)
  Diameter = false
  Dimline = (800,-5250,0)
  Direction = (0,0,0)
  Distance = 3400
  End = (800,-5250,0)
  Normal = (0,0,1)
  Start = (800,-1850,0)
FEATURE [App::FeaturePython] Dimension023  # Draft dimension (typed FeaturePython)
  Diameter = false
  Dimline = (800,-5250,0)
  Direction = (0,0,0)
  Distance = 250
  End = (800,-5500,0)
  Normal = (0,0,1)
  Start = (800,-5250,0)
FEATURE [App::FeaturePython] Dimension025  # Draft dimension (typed FeaturePython)
  Diameter = false
  Dimline = (2550.74,-5617.71,0)
  Direction = (0,0,0)
  Distance = 500
  End = (2405,-5250,0)
  Normal = (0,0,1)
  Start = (2405,-5750,0)
FEATURE [App::FeaturePython] Dimension026  # Draft dimension (typed FeaturePython)
  Diameter = false
  Dimline = (2550.74,-5617.71,0)
  Direction = (0,0,0)
  Distance = 5000
  End = (2405,-250,0)
  Normal = (0,0,1)
  Start = (2405,-5250,0)
FEATURE [App::FeaturePython] Dimension027  # Draft dimension (typed FeaturePython)
  Diameter = false
  Dimline = (2550.74,-5617.71,0)
  Direction = (0,0,0)
  Distance = 250
  End = (2405,-0.00016282,0)
  Normal = (0,0,1)
  Start = (2405,-250,0)
FEATURE [App::FeaturePython] Dimension028  # Draft dimension (typed FeaturePython)
  Diameter = false
  Dimline = (-748.438,-4857.61,0)
  Direction = (0,0,0)
  Distance = 3500
  End = (9.999e-09,-5350,0)
  Normal = (0,0,1)
  Start = (-3500,-5350,0)
FEATURE [App::FeaturePython] Dimension029  # Draft dimension (typed FeaturePython)
  Diameter = false
  Dimline = (-748.438,-4857.61,0)
  Direction = (0,0,0)
  Distance = 150
  End = (150,-5350,0)
  Normal = (0,0,1)
  Start = (9.999e-09,-5350,0)
FEATURE [App::FeaturePython] Dimension030  # Draft dimension (typed FeaturePython)
  Diameter = false
  Dimline = (-748.438,-4857.61,0)
  Direction = (0,0,0)
  Distance = 7900
  End = (8050,-5350,0)
  Normal = (0,0,1)
  Start = (150,-5350,0)
FEATURE [App::FeaturePython] Dimension031  # Draft dimension (typed FeaturePython)
  Diameter = false
  Dimline = (-748.438,-4857.61,0)
  Direction = (0,0,0)
  Distance = 150
  End = (8200,-5350,0)
  Normal = (0,0,1)
  Start = (8050,-5350,0)
FEATURE [App::FeaturePython] Dimension032  # Draft dimension (typed FeaturePython)
  Diameter = false
  Dimline = (8200,-4857.61,0)
  Direction = (0,0,0)
  Distance = 1650
  End = (9850,-5350,0)
  Normal = (0,0,1)
  Start = (8200,-5350,0)
FEATURE [App::FeaturePython] Dimension033  # Draft dimension (typed FeaturePython)
  Diameter = false
  Dimline = (9850,-4857.61,0)
  Direction = (0,0,0)
  Distance = 150
  End = (10000,-5350,0)
  Normal = (0,0,1)
  Start = (9850,-5350,0)
FEATURE [App::FeaturePython] Dimension035  # Draft dimension (typed FeaturePython)
  Diameter = false
  Dimline = (-4500,-5500,0)
  Direction = (0,0,0)
  Distance = 5500
  End = (-4000,-0.00016282,0)
  Normal = (0,0,1)
  Start = (-4000,-5500,0)
FEATURE [App::FeaturePython] Dimension036  # Draft dimension (typed FeaturePython)
  Diameter = false
  Dimline = (11000,-850,0)
  Direction = (0,0,0)
  Distance = 5500
  End = (10000,-0.00016282,0)
  Normal = (0,0,1)
  Start = (10000,-5500,0)
FEATURE [App::FeaturePython] Dimension037  # Draft dimension (typed FeaturePython)
  Diameter = false
  Dimline = (328.42,-2254.64,0)
  Direction = (0,0,0)
  Distance = 150
  End = (150,-1850,0)
  Normal = (0,0,1)
  Start = (9.999e-09,-1850,0)
FEATURE [App::FeaturePython] Dimension038  # Draft dimension (typed FeaturePython)
  Diameter = false
  Dimline = (328.42,-2254.64,0)
  Direction = (0,0,0)
  Distance = 1200
  End = (1350,-1850,0)
  Normal = (0,0,1)
  Start = (150,-1850,0)
FEATURE [App::FeaturePython] Dimension039  # Draft dimension (typed FeaturePython)
  Diameter = false
  Dimline = (328.42,-2254.64,0)
  Direction = (0,0,0)
  Distance = 1400
  End = (2750,-1850,0)
  Normal = (0,0,1)
  Start = (1350,-1850,0)
FEATURE [App::FeaturePython] Dimension040  # Draft dimension (typed FeaturePython)
  Diameter = false
  Dimline = (328.42,-2254.64,0)
  Direction = (0,0,0)
  Distance = 1700
  End = (4450,-1850,0)
  Normal = (0,0,1)
  Start = (2750,-1850,0)
FEATURE [App::FeaturePython] Dimension041  # Draft dimension (typed FeaturePython)
  Diameter = false
  Dimline = (328.42,-2254.64,0)
  Direction = (0,0,0)
  Distance = 800
  End = (5250,-1850,0)
  Normal = (0,0,1)
  Start = (4450,-1850,0)
FEATURE [App::FeaturePython] Dimension042  # Draft dimension (typed FeaturePython)
  Diameter = false
  Dimline = (328.42,-2254.64,0)
  Direction = (0,0,0)
  Distance = 1200
  End = (6450,-1850,0)
  Normal = (0,0,1)
  Start = (5250,-1850,0)
FEATURE [App::FeaturePython] Dimension043  # Draft dimension (typed FeaturePython)
  Diameter = false
  Dimline = (328.42,-2254.64,0)
  Direction = (0,0,0)
  Distance = 800
  End = (7250,-1850,0)
  Normal = (0,0,1)
  Start = (6450,-1850,0)
FEATURE [App::FeaturePython] Dimension044  # Draft dimension (typed FeaturePython)
  Diameter = false
  Dimline = (328.42,-2254.64,0)
  Direction = (0,0,0)
  Distance = 800
  End = (8050,-1850,0)
  Normal = (0,0,1)
  Start = (7250,-1850,0)
FEATURE [App::FeaturePython] Dimension045  # Draft dimension (typed FeaturePython)
  Diameter = false
  Dimline = (328.42,-2254.64,0)
  Direction = (0,0,0)
  Distance = 150
  End = (8200,-1850,0)
  Normal = (0,0,1)
  Start = (8050,-1850,0)
FEATURE [App::FeaturePython] Dimension046  # Draft dimension (typed FeaturePython)
  Diameter = false
  Dimline = (328.42,-2254.64,0)
  Direction = (0,0,0)
  Distance = 1650
  End = (9850,-1850,0)
  Normal = (0,0,1)
  Start = (8200,-1850,0)
FEATURE [App::FeaturePython] Dimension047  # Draft dimension (typed FeaturePython)
  Diameter = false
  Dimline = (328.42,-2254.64,0)
  Direction = (0,0,0)
  Distance = 150
  End = (10000,-1850,0)
  Normal = (0,0,1)
  Start = (9850,-1850,0)
FEATURE [App::FeaturePython] Dimension048  # Draft dimension (typed FeaturePython)
  Diameter = false
  Dimline = (360.611,-4431.24,0)
  Direction = (0,0,0)
  Distance = 150
  End = (150,-5350,0)
  Normal = (0,0,1)
  Start = (9.999e-09,-5350,0)
FEATURE [App::FeaturePython] Dimension050  # Draft dimension (typed FeaturePython)
  Diameter = false
  Dimline = (360.611,-4431.24,0)
  Direction = (0,0,0)
  Distance = 50
  End = (5233.23,-5350,0)
  Normal = (0,0,1)
  Start = (5183.23,-5350,0)
FEATURE [App::FeaturePython] Dimension051  # Draft dimension (typed FeaturePython)
  Diameter = false
  Dimline = (360.611,-4431.24,0)
  Direction = (0,0,0)
  Distance = 2816.77
  End = (8050,-5350,0)
  Normal = (0,0,1)
  Start = (5233.23,-5350,0)
FEATURE [App::FeaturePython] Dimension052  # Draft dimension (typed FeaturePython)
  Diameter = false
  Dimline = (360.611,-4431.24,0)
  Direction = (0,0,0)
  Distance = 150
  End = (8200,-5350,0)
  Normal = (0,0,1)
  Start = (8050,-5350,0)
FEATURE [App::FeaturePython] Dimension053  # Draft dimension (typed FeaturePython)
  Diameter = false
  Dimline = (360.611,-4431.24,0)
  Direction = (0,0,0)
  Distance = 1650
  End = (9850,-5350,0)
  Normal = (0,0,1)
  Start = (8200,-5350,0)
FEATURE [App::FeaturePython] Dimension054  # Draft dimension (typed FeaturePython)
  Diameter = false
  Dimline = (360.611,-4431.24,0)
  Direction = (0,0,0)
  Distance = 150
  End = (10000,-5350,0)
  Normal = (0,0,1)
  Start = (9850,-5350,0)
FEATURE [Part::FeaturePython] Panel  label="Paviment"  # WARN: FeaturePython — macro-defined, semantics opaque (R4)
  Area = 3.841e+07
  Base = -> DWire
  FaceMaker = 0
  HorizontalArea = 0
  Length = 0
  Material = -> Material004
  MoveWithHost = false
  Normal = (0,0,0)
  PerimeterLength = 0
  Role = 4
  Sheets = 1
  Thickness = 100
  VerticalArea = 0
  WaveDirection = 0
  WaveHeight = 0
  WaveLength = 0
  WaveType = 0
  Width = 0
FEATURE [App::DocumentObjectGroup] Group  label="Acabats"
  Group = -> [Panel]
FEATURE [App::FeaturePython] Section001  label="S_Planta Coberta"  # WARN: FeaturePython — macro-defined, semantics opaque (R4)
  Objects = -> [Wall002,Window002,Wall001,Window,Window001,Group006,Group,Component,Component003,Component004,Group008,Floor001]
  OnlySolids = true
  Placement = pos=(3500,-3000,4000) rot=(0,0,1;0rad)
FEATURE [App::FeaturePython] Section002  label="S_Secció Longitudinal"  # WARN: FeaturePython — macro-defined, semantics opaque (R4)
  Objects = -> [Wall002,Window002,Wall001,Window,Window001,Component,Component003,Component004,Group005,Group006,Group,Group008,Floor001]
  OnlySolids = true
  Placement = pos=(3000,-4000,1000) rot=(1,0,0;1.5708rad)
FEATURE [App::FeaturePython] Section003  label="S_Secció Transversal"  # WARN: FeaturePython — macro-defined, semantics opaque (R4)
  Objects = -> [Wall002,Window002,Wall001,Window,Window001,Component,Component003,Component004,Group005,Group006,Group,Group008,Floor001]
  OnlySolids = true
  Placement = pos=(3000,-3000,1000) rot=(0.57735,0.57735,0.57735;2.0944rad)
FEATURE [Part::Part2DObjectPython] Rectangle087  # Draft 2D object (typed FeaturePython)
  ChamferSize = 0
  Columns = 1
  FilletRadius = 0
  Height = 3400
  Length = 7900
  MakeFace = true
  Placement = pos=(150,-5250,0) rot=(0,0,1;0rad)
  Rows = 1
FEATURE [Part::Extrusion] Extrusion003  label="Sala_base"
  Base = -> Rectangle087
  Dir = (0,0,2500)
  DirMode = 0
  FaceMakerClass = Part::FaceMakerBullseye
  LengthFwd = 0
  LengthRev = 0
  Solid = true
  Symmetric = false
FEATURE [Part::FeaturePython] Space  label="Sala"  # WARN: FeaturePython — macro-defined, semantics opaque (R4)
  Area = 2.686e+07
  AutoPower = false
  Base = -> Extrusion003
  Conditioning = 5
  EquipmentPower = 0
  FloorThickness = 0
  HorizontalArea = 0
  LightingPower = 0
  MoveWithHost = false
  NumberOfPeople = 0
  PerimeterLength = 22600
  Role = 1
  SpaceType = 37
  VerticalArea = 5.65e+07
FEATURE [Part::Part2DObjectPython] DWire008  # Draft 2D object (typed FeaturePython)
  ChamferSize = 0
  Closed = true
  End = (250,-1750,0)
  FilletRadius = 0
  Length = 10400
  MakeFace = true
  Points = (8) [(250,-250,0),(3850,-250,0),(3850,-1750,0),(2750,-1750,0),(2750,-1850,0),(1350,-1850,0),(1350,-1750,0),(250,-1750,0)]
  Start = (250,-250,0)
  Subdivisions = 0
FEATURE [Part::Extrusion] Extrusion004  label="Cuina_base"
  Base = -> DWire008
  Dir = (0,0,2500)
  DirMode = 0
  FaceMakerClass = Part::FaceMakerBullseye
  LengthFwd = 0
  LengthRev = 0
  Solid = true
  Symmetric = false
FEATURE [Part::FeaturePython] Space001  label="Cuina"  # WARN: FeaturePython — macro-defined, semantics opaque (R4)
  Area = 5.54e+06
  AutoPower = false
  Base = -> Extrusion004
  Conditioning = 0
  EquipmentPower = 0
  FloorThickness = 0
  HorizontalArea = 0
  LightingPower = 0
  MoveWithHost = false
  NumberOfPeople = 0
  PerimeterLength = 10400
  Role = 1
  SpaceType = 33
  VerticalArea = 26000000
FEATURE [Part::Part2DObjectPython] DWire009  # Draft 2D object (typed FeaturePython)
  ChamferSize = 0
  Closed = true
  End = (3950,-1750,0)
  FilletRadius = 0
  Length = 6800
  MakeFace = true
  Points = (8) [(3950,-250,0),(5750,-250,0),(5750,-1750,0),(5250,-1750,0),(5250,-1850,0),(4450,-1850,0),(4450,-1750,0),(3950,-1750,0)]
  Start = (3950,-250,0)
  Subdivisions = 0
FEATURE [Part::Extrusion] Extrusion005  label="Magatzem_base"
  Base = -> DWire009
  Dir = (0,0,2500)
  DirMode = 0
  FaceMakerClass = Part::FaceMakerBullseye
  LengthFwd = 0
  LengthRev = 0
  Solid = true
  Symmetric = false
FEATURE [Part::FeaturePython] Space002  label="Magatzem"  # WARN: FeaturePython — macro-defined, semantics opaque (R4)
  Area = 2.78e+06
  AutoPower = false
  Base = -> Extrusion005
  Conditioning = 0
  EquipmentPower = 0
  FloorThickness = 0
  HorizontalArea = 0
  LightingPower = 0
  MoveWithHost = false
  NumberOfPeople = 0
  PerimeterLength = 6800
  Role = 1
  SpaceType = 36
  VerticalArea = 17000000
FEATURE [Part::Part2DObjectPython] DWire010  # Draft 2D object (typed FeaturePython)
  ChamferSize = 0
  Closed = true
  End = (5850,-1750,0)
  FilletRadius = 0
  Length = 7400
  MakeFace = true
  Points = (8) [(5850,-250,0),(7950,-250,0),(7950,-1750,0),(7250,-1750,0),(7250,-1850,0),(6450,-1850,0),(6450,-1750,0),(5850,-1750,0)]
  Start = (5850,-250,0)
  Subdivisions = 0
FEATURE [Part::Extrusion] Extrusion006  label="Bany_base"
  Base = -> DWire010
  Dir = (0,0,2500)
  DirMode = 0
  FaceMakerClass = Part::FaceMakerBullseye
  LengthFwd = 0
  LengthRev = 0
  Solid = true
  Symmetric = false
FEATURE [Part::FeaturePython] Space003  label="Bany"  # WARN: FeaturePython — macro-defined, semantics opaque (R4)
  Area = 3230000
  AutoPower = false
  Base = -> Extrusion006
  Conditioning = 0
  EquipmentPower = 0
  FloorThickness = 0
  HorizontalArea = 0
  LightingPower = 0
  MoveWithHost = false
  NumberOfPeople = 0
  PerimeterLength = 7400
  Role = 1
  SpaceType = 35
  VerticalArea = 1.85e+07
FEATURE [App::DocumentObjectGroup] Group014  label="Espais"
  Group = -> [Space,Space001,Space002,Space003]
FEATURE [App::DocumentObjectGroupPython] Floor  label="Planta"  # scripted group (container) (typed FeaturePython)
  Area = 3.841e+07
  Group = -> [Group002,Group003,Group004,Group005,Group006,Group,Group008,Group014]
  Height = 2500
FEATURE [App::DocumentObjectGroupPython] Building  label="Edifici"  # scripted group (container) (typed FeaturePython)
  Area = 0
  BuildingType = 1
  Group = -> [Floor,Floor001]
  Height = 0
FEATURE [Part::FeaturePython] Site  label="Font de Ribes"  # WARN: FeaturePython — macro-defined, semantics opaque (R4)
  AdditionVolume = 0
  Address = Font de Ribes
  Area = 0
  City = Montblanc
  Country = Catalunya
  Elevation = 418600
  ExtrusionVector = (0,0,-100000)
  Group = -> [Building]
  Height = 0
  Latitude = 0
  Longitude = 0
  NorthDeviation = 0
  Perimeter = 0
  PostalCode = 43400
  ProjectedArea = 0
  RemoveSplitter = false
  SubtractionVolume = 0
FEATURE [TechDraw::DrawSVGTemplate] Template
  Height = 210
  Orientation = 1
  Width = 297
FEATURE [TechDraw::DrawViewArch] ArchView001  label="V_Planta Coberta"
  AllOn = false
  FontSize = 12
  LineWidth = 0.1
  LockPosition = false
  RenderMode = 0
  Rotation = 0
  Scale = 0.01
  ScaleType = 2
  ShowFill = true
  ShowHidden = false
  Source = -> Section001
  Symbol = <blob: 2674 chars omitted>
  X = 220
  Y = 170
FEATURE [TechDraw::DrawViewArch] ArchView002  label="V_Secció Longitudinal"
  AllOn = false
  FontSize = 12
  LineWidth = 0.1
  LockPosition = false
  RenderMode = 0
  Rotation = -90
  Scale = 0.01
  ScaleType = 2
  ShowFill = true
  ShowHidden = false
  Source = -> Section002
  Symbol = <blob: 20969 chars omitted>
  X = 91.5
  Y = 105
FEATURE [TechDraw::DrawViewArch] ArchView003  label="V Secció Transversal"
  AllOn = false
  FontSize = 12
  LineWidth = 0.1
  LockPosition = false
  RenderMode = 0
  Rotation = 90
  Scale = 0.01
  ScaleType = 2
  ShowFill = true
  ShowHidden = false
  Source = -> Section003
  Symbol = <blob: 14822 chars omitted>
  X = 185
  Y = 105
FEATURE [Part::Feature] Compound042  label="Mobiliari planta"
  Placement = pos=(0,2.5e-08,0) rot=(0,0,1;0rad)
  shape: bbox 7700 x 5000 x 2e-07 mm, 37 faces, 0 solids (baked)
FEATURE [App::FeaturePython] Section006  label="S_Alçat_Oest"  # WARN: FeaturePython — macro-defined, semantics opaque (R4)
  Objects = -> [Site,Wall002,Window002,Wall001,Window,Window001,Group006,Group,Group008,Floor001,Component,Component003,Component004,Group005]
  OnlySolids = true
  Placement = pos=(10474.1,-3000,1000) rot=(0.57735,0.57735,0.57735;2.0944rad)
FEATURE [App::FeaturePython] Section007  label="S_Alçat_Est"  # WARN: FeaturePython — macro-defined, semantics opaque (R4)
  Objects = -> [Wall002,Window002,Wall001,Window,Window001,Component,Component003,Component004,Group005,Group006,Group,Group008,Floor001]
  OnlySolids = true
  Placement = pos=(-3957.38,-3000,1000) rot=(0,1,0;-1.5708rad)
FEATURE [TechDraw::DrawViewArch] ArchView005  label="V_Alçat Est"
  AllOn = false
  FontSize = 12
  LineWidth = 0.1
  LockPosition = false
  RenderMode = 0
  Rotation = -90
  Scale = 0.01
  ScaleType = 2
  ShowFill = true
  ShowHidden = false
  Source = -> Section007
  Symbol = <blob: 4372 chars omitted>
  X = 185
  Y = 50
FEATURE [TechDraw::DrawViewAnnotation] Annotation  label="T_Planta Baixa"
  Font = Century Gothic
  LineSpace = 80
  LockPosition = false
  MaxWidth = -1
  Rotation = 0
  ScaleType = 0
  Text = Default Text
  TextSize = 3
  TextStyle = 0
  X = 19.6685
  Y = 204.809
FEATURE [App::FeaturePython] Dimension  # Draft dimension (typed FeaturePython)
  Diameter = false
  Dimline = (5183.23,-4431.24,0)
  Direction = (0,0,0)
  Distance = 5033.23
  End = (5183.23,-5350,0)
  Normal = (0,0,1)
  Start = (150,-5350,0)
FEATURE [App::FeaturePython] Dimension056  # Draft dimension (typed FeaturePython)
  Diameter = false
  Dimline = (-4000,-5500,0)
  Direction = (0,0,0)
  Distance = 1850
  End = (4.999e-09,4.9997e-08,2500)
  LinkedGeometry = -> [Wall001]
  Normal = (0,0,1)
  Start = (4.999e-09,-1850,2500)
  Support = -> Wall001
FEATURE [App::FeaturePython] Dimension057  # Draft dimension (typed FeaturePython)
  Diameter = false
  Dimline = (-4000,-5500,0)
  Direction = (0,0,0)
  Distance = 3500
  End = (1e-12,-1850,2500)
  LinkedGeometry = -> [Window001]
  Normal = (0,0,1)
  Start = (1e-12,-5350,2500)
  Support = -> Window001
FEATURE [App::FeaturePython] Dimension058  # Draft dimension (typed FeaturePython)
  Diameter = false
  Dimline = (10500,-5500,0)
  Direction = (0,0,0)
  Distance = 3650
  End = (10000,-1850,2500)
  LinkedGeometry = -> [Wall002]
  Normal = (0,0,1)
  Start = (10000,-5500,2500)
  Support = -> Wall002
FEATURE [App::FeaturePython] Dimension059  # Draft dimension (typed FeaturePython)
  Diameter = false
  Dimline = (8700,5.0001e-08,0)
  Direction = (0,0,0)
  Distance = 1950
  End = (8200,-1950,2500)
  LinkedGeometry = -> [Wall001]
  Normal = (0,0,1)
  Start = (8200,4.9997e-08,2500)
  Support = -> Wall001
FEATURE [App::DocumentObjectGroup] Group007  label="Anotacions"
  Group = -> [Arc,Compound042,Group012]
FEATURE [App::FeaturePython] Section  label="S_Planta Baixa"  # WARN: FeaturePython — macro-defined, semantics opaque (R4)
  Objects = -> [Group003,Group004,Group005,Group006,Group,Group008,Floor001,Window002,Window,Window001,Compound042,Group012,Space,Space002,Space001,Space003]
  OnlySolids = true
  Placement = pos=(3500,-3000,1200) rot=(0,0,1;0rad)
FEATURE [App::DocumentObjectGroup] Group010  label="Seccions"
  Group = -> [Section,Section001,Section002,Section003,Section004,Section005,Section006,Section007]
FEATURE [Part::Part2DObjectPython] Shape2DView001  label="Planta Baixa_Tall"  # Draft 2D object (typed FeaturePython)
  Base = -> Section
  HiddenLines = false
  InPlace = true
  Placement = pos=(1e-12,-8737.29,-1200) rot=(0,0,1;0rad)
  Projection = (0.57735,-0.57735,0.57735)
  ProjectionMode = 2
  SegmentLength = 0.05
  Tessellation = false
  VisibleOnly = false
FEATURE [Part::Part2DObjectPython] Shape2DView002  label="Planta Baixa_Projecció"  # Draft 2D object (typed FeaturePython)
  Base = -> Section
  HiddenLines = false
  InPlace = true
  Placement = pos=(2e-12,-8737.29,0) rot=(0,0,1;0rad)
  Projection = (0.57735,-0.57735,0.57735)
  ProjectionMode = 0
  SegmentLength = 0.05
  Tessellation = false
  VisibleOnly = false
FEATURE [App::DocumentObjectGroup] Group011  label="shape 2D views"
  Group = -> [Shape2DView001,Shape2DView002]
FEATURE [App::FeaturePython] Dimension013  # Draft dimension (typed FeaturePython)
  Diameter = false
  Dimline = (-3500,-6000,0)
  Direction = (0,0,0)
  Distance = 5875
  End = (-3500,-14237.3,0)
  LinkedGeometry = -> [Shape2DView001]
  Normal = (0,0,1)
  Start = (2375,-14237.3,0)
  Support = -> Shape2DView001
FEATURE [App::FeaturePython] Dimension015  # Draft dimension (typed FeaturePython)
  Diameter = false
  Dimline = (5225,-6000,0)
  Direction = (0,0,0)
  Distance = 4775
  End = (5225,-14237.3,0)
  LinkedGeometry = -> [Shape2DView001]
  Normal = (0,0,1)
  Start = (10000,-14237.3,0)
  Support = -> Shape2DView001
FEATURE [App::DocumentObjectGroup] Group012  label="Cotes_Planta Baixa"
  Group = -> [Dimension004,Dimension005,Dimension006,Dimension007,Dimension008,Dimension009,Dimension010,Dimension011,Dimension012,Dimension013,Dimension014,Dimension015,Dimension017,Dimension018,Dimension019,Dimension020,Dimension021,Dimension022,Dimension023,Dimension025,Dimension026,Dimension027,Dimension028,Dimension029,Dimension030,Dimension031,Dimension032,Dimension033,Dimension035,Dimension036,+23 more]
FEATURE [App::FeaturePython] Dimension055  # Draft dimension (typed FeaturePython)
  Diameter = false
  Dimline = (8200,500,0)
  Direction = (0,0,0)
  Distance = 8200
  End = (5.001e-09,-8737.29,0)
  LinkedGeometry = -> [Shape2DView001]
  Normal = (0,0,1)
  Start = (8200,-8737.29,0)
  Support = -> Shape2DView001
FEATURE [App::DocumentObjectGroup] Group015  label="Plànols"
  Group = -> [Page]
FEATURE [TechDraw::DrawPage] Page  label="01_DF_A4"
  KeepUpdated = true
  ProjectionType = 0
  Template = -> Template
  Views = -> [ArchView,ArchView001,ArchView002,ArchView003,ArchView004,ArchView005,Annotation]
FEATURE [TechDraw::DrawViewArch] ArchView  label="V_Planta Baixa"
  AllOn = false
  FontSize = 3
  LineWidth = 0.1
  LockPosition = false
  RenderMode = 0
  Rotation = 0
  Scale = 0.01
  ScaleType = 2
  ShowFill = true
  ShowHidden = false
  Source = -> Section
  Symbol = <blob: 150053 chars omitted>
  X = 71.3813
  Y = 162.504
FEATURE [App::FeaturePython] Section004  label="S_Alçat Sud"  # WARN: FeaturePython — macro-defined, semantics opaque (R4)
  Objects = -> [Compound042,DWire010,Extrusion006,DWire009,Extrusion005,Rectangle014,Rectangle017,Rectangle019,Rectangle064,Rectangle073,Rectangle074,Rectangle075,Arc,DWire007,Rectangle,Wall,Wall001,Wall002,Wall003,Rectangle047,Wall004,Extrusion,Component,Extrusion001,Component003,Extrusion002,Component004,Component006,Component007,Component008,Site,Structure,DWire,Structure001,Structure002,Structure003,Wall007,+35 more]
  OnlySolids = true
  Placement = pos=(3000,-5819.7,1000) rot=(1,0,0;1.5708rad)
FEATURE [App::FeaturePython] Section005  label="S_Alçat Nord"  # WARN: FeaturePython — macro-defined, semantics opaque (R4)
  Objects = -> [Compound042,DWire010,Extrusion006,DWire009,Extrusion005,Rectangle014,Rectangle017,Rectangle019,Rectangle064,Rectangle073,Rectangle074,Rectangle075,Arc,DWire007,Rectangle,Wall,Wall001,Wall002,Wall003,Rectangle047,Wall004,Extrusion,Component,Extrusion001,Component003,Extrusion002,Component004,Component006,Component007,Component008,Site,Structure,DWire,Structure001,Structure002,Structure003,Wall007,+35 more]
  OnlySolids = true
  Placement = pos=(3000,1021.61,1000) rot=(-1,0,0;1.5708rad)
FEATURE [TechDraw::DrawViewArch] ArchView004  label="V_Alçat Sud_"
  AllOn = false
  FontSize = 12
  LineWidth = 0.1
  LockPosition = false
  RenderMode = 0
  Rotation = -90
  Scale = 0.01
  ScaleType = 2
  ShowFill = true
  ShowHidden = false
  Source = -> Section004
  Symbol = <blob: 268810 chars omitted>
  X = 75
  Y = 50
